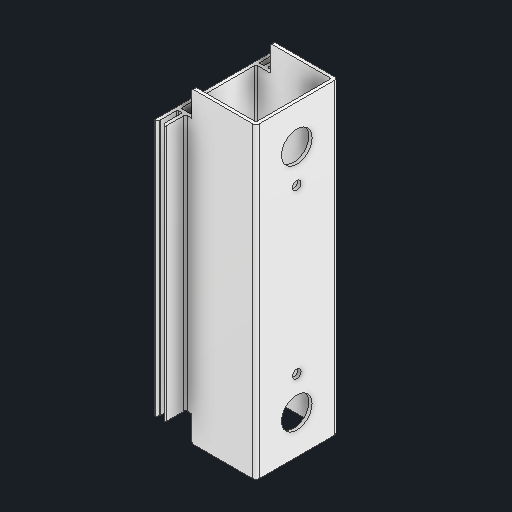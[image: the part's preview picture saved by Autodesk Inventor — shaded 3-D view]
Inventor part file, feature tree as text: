
AUTODESK INVENTOR PART (.ipt)
format: ipt  version: 2025 (Build 290162000, 162)  size: 144,896 bytes
history: native  units: in
note: dims shown in document units (in); Inventor stores cm internally (conversion verified against a paired STEP export)
features: fillet x1
ambient origin geometry x8: Origin, YZ Plane, XZ Plane, XY Plane, X Axis, Y Axis, Z Axis, Center Point
bodies: Solid1 (feature_tree)
feature tree (1):
  fillet  "Fillet7"  [1 undecoded]
note: 1 required parameter value undecoded (feature->parameter linkage not recoverable at this tier; creation-order binding heuristic only, values carry confidence <= 0.55)
